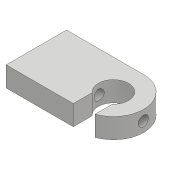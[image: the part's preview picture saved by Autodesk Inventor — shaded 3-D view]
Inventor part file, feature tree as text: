
AUTODESK INVENTOR PART (.ipt)
format: ipt  version: 2017 (Build 210142000, 142)  size: 119,296 bytes
history: native  units: mm
features: extrude x4, sketch x4, plane x1
ambient origin geometry x8: Origin, YZ Plane, XZ Plane, XY Plane, X Axis, Y Axis, Z Axis, Center Point
bodies: Solid1 (feature_tree)
feature tree (9):
  extrude  "Extrusion1"  Depth=18.0mm
  extrude  "Extrusion2"  Depth=9.0mm
  extrude  "Extrusion3"  Depth=6.0mm
  plane  "Work Plane1"
  extrude  "Extrusion4"  Depth=10.0mm TaperAngle=0.0deg
  sketch  "Sketch1"  dims[d0=23.0mm d1=18.0mm]
  sketch  "Sketch2"  dims[d2=9.0mm d3=9.0mm]
  sketch  "Sketch3"  dims[d4=6.0mm d5=0.0mm d6=3.0mm]
  sketch  "Sketch4"  dims[d7=3.0mm d8=5.0mm d9=0.0mm d10=6.0mm d11=6.0mm d12=10.0mm d13=0.0mm d14=-32.0mm d15=3.0mm d16=18.0mm d17=0.0mm]
